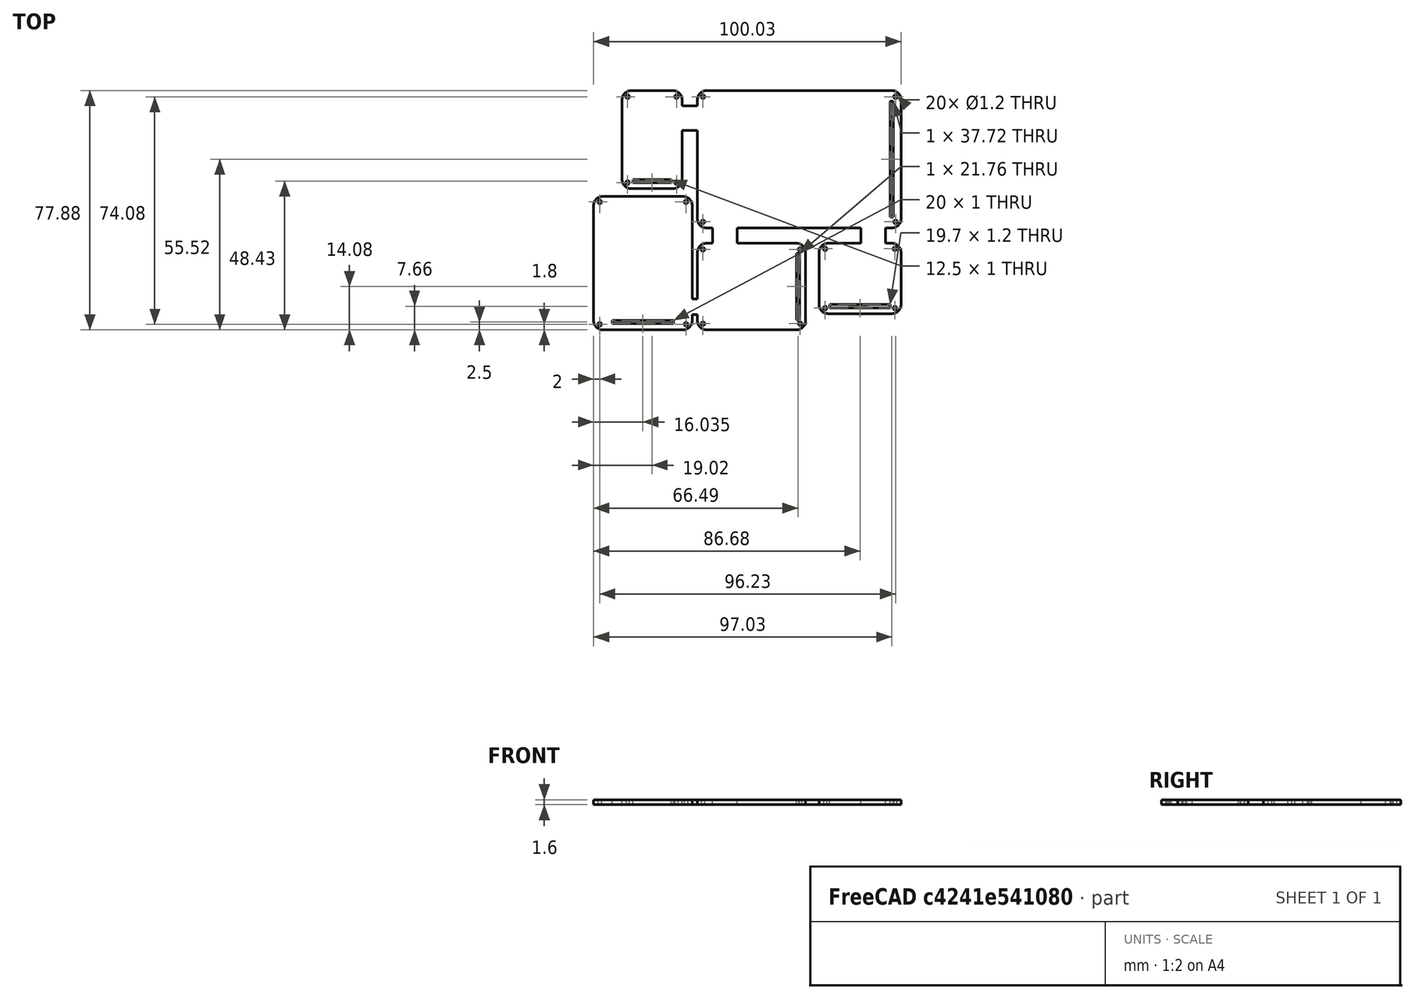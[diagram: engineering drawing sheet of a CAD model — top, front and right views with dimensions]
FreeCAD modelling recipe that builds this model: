
FCSTD DOCUMENT  (FreeCAD 0.21R33771 (Git))
Label: UINIO-Monitor
License: All rights reserved
LicenseURL: http://en.wikipedia.org/wiki/All_rights_reserved
objects: Sketcher::SketchObject×1, PartDesign::Pad×1, PartDesign::Body×1
note: 4 computed .brp shape members not serialized (recipe doc carries the construction recipe); baked Part::Feature solids carry a one-line shape summary decoded from their .brp

FEATURE [Sketcher::SketchObject] Sketch
  FullyConstrained = false
  MapMode = 5
  Support = -> [XY_Plane]
  sketch-geometry (140):
    g0: Circle CenterX=-31.33 CenterY=20.36 CenterZ=0 NormalX=0 NormalY=0 NormalZ=1 AngleXU=0 Radius=0.875
    g1: Circle CenterX=-31.33 CenterY=20.36 CenterZ=0 NormalX=0 NormalY=0 NormalZ=1 AngleXU=0 Radius=0.6
    g2: LineSegment StartX=-30.13 StartY=21.36 StartZ=0 EndX=30.13 EndY=21.36 EndZ=0
    g3: LineSegment StartX=30.13 StartY=21.36 StartZ=0 EndX=30.13 EndY=-21.36 EndZ=0
    g4: LineSegment StartX=30.13 StartY=-21.36 StartZ=0 EndX=-30.13 EndY=-21.36 EndZ=0
    g5: LineSegment StartX=-30.13 StartY=-21.36 StartZ=0 EndX=-30.13 EndY=21.36 EndZ=0
    g6: LineSegment StartX=-30.13 StartY=22.36 StartZ=0 EndX=30.13 EndY=22.36 EndZ=0
    g7: LineSegment StartX=-30.13 StartY=-22.36 StartZ=0 EndX=30.13 EndY=-22.36 EndZ=0
    g8: LineSegment StartX=33.13 StartY=19.36 StartZ=0 EndX=33.13 EndY=-19.36 EndZ=0
    g9: ArcOfCircle CenterX=30.13 CenterY=19.36 CenterZ=0 NormalX=0 NormalY=0 NormalZ=1 AngleXU=0 Radius=3 StartAngle=0 EndAngle=1.5708
    g10: ArcOfCircle CenterX=30.13 CenterY=-19.36 CenterZ=0 NormalX=0 NormalY=0 NormalZ=1 AngleXU=0 Radius=3 StartAngle=4.71239 EndAngle=6.28319
    g11: ArcOfCircle CenterX=-30.13 CenterY=-19.36 CenterZ=0 NormalX=0 NormalY=0 NormalZ=1 AngleXU=0 Radius=3 StartAngle=3.14159 EndAngle=4.71239
    g12: ArcOfCircle CenterX=-30.13 CenterY=19.3596 CenterZ=0 NormalX=0 NormalY=0 NormalZ=1 AngleXU=0 Radius=3.00035 StartAngle=1.5708 EndAngle=3.12625
    g13: LineSegment StartX=29.63 StartY=18.86 StartZ=0 EndX=30.63 EndY=18.86 EndZ=0
    g14: LineSegment StartX=30.63 StartY=18.86 StartZ=0 EndX=30.63 EndY=-18.86 EndZ=0
    g15: LineSegment StartX=30.63 StartY=-18.86 StartZ=0 EndX=29.63 EndY=-18.86 EndZ=0
    g16: LineSegment StartX=29.63 StartY=-18.86 StartZ=0 EndX=29.63 EndY=18.86 EndZ=0
    g17: Circle CenterX=-31.33 CenterY=-20.36 CenterZ=0 NormalX=0 NormalY=0 NormalZ=1 AngleXU=0 Radius=0.875
    g18: Circle CenterX=-31.33 CenterY=-20.36 CenterZ=0 NormalX=0 NormalY=0 NormalZ=1 AngleXU=0 Radius=0.6
    g19: Circle CenterX=31.33 CenterY=20.36 CenterZ=0 NormalX=0 NormalY=0 NormalZ=1 AngleXU=0 Radius=0.875
    g20: Circle CenterX=31.33 CenterY=20.36 CenterZ=0 NormalX=0 NormalY=0 NormalZ=1 AngleXU=0 Radius=0.6
    g21: Circle CenterX=31.33 CenterY=-20.36 CenterZ=0 NormalX=0 NormalY=0 NormalZ=1 AngleXU=0 Radius=0.875
    g22: Circle CenterX=31.33 CenterY=-20.36 CenterZ=0 NormalX=0 NormalY=0 NormalZ=1 AngleXU=0 Radius=0.6
    g23: LineSegment StartX=-30.13 StartY=-28.36 StartZ=0 EndX=-0.91 EndY=-28.36 EndZ=0
    g24: LineSegment StartX=-0.91 StartY=-28.36 StartZ=0 EndX=-0.91 EndY=-54.52 EndZ=0
    g25: LineSegment StartX=-0.91 StartY=-54.52 StartZ=0 EndX=-30.13 EndY=-54.52 EndZ=0
    g26: LineSegment StartX=-30.13 StartY=-54.52 StartZ=0 EndX=-30.13 EndY=-28.36 EndZ=0
    g27: LineSegment StartX=7.43 StartY=-30.36 StartZ=0 EndX=32.13 EndY=-30.36 EndZ=0
    g28: LineSegment StartX=32.13 StartY=-30.36 StartZ=0 EndX=32.13 EndY=-47.26 EndZ=0
    g29: LineSegment StartX=32.13 StartY=-47.26 StartZ=0 EndX=7.43 EndY=-47.26 EndZ=0
    g30: LineSegment StartX=7.43 StartY=-47.26 StartZ=0 EndX=7.43 EndY=-30.36 EndZ=0
    g31: LineSegment StartX=-30.13 StartY=-27.36 StartZ=0 EndX=-0.91 EndY=-27.36 EndZ=0
    g32: LineSegment StartX=2.09 StartY=-30.36 StartZ=0 EndX=2.09 EndY=-52.52 EndZ=0
    g33: LineSegment StartX=-30.13 StartY=-55.52 StartZ=0 EndX=-0.91 EndY=-55.52 EndZ=0
    g34: ArcOfCircle CenterX=-0.91 CenterY=-30.36 CenterZ=0 NormalX=0 NormalY=0 NormalZ=1 AngleXU=0 Radius=3 StartAngle=0 EndAngle=1.5708
    g35: ArcOfCircle CenterX=-0.91 CenterY=-52.52 CenterZ=0 NormalX=0 NormalY=0 NormalZ=1 AngleXU=0 Radius=3 StartAngle=4.71239 EndAngle=6.28319
    g36: ArcOfCircle CenterX=-30.13 CenterY=-52.52 CenterZ=0 NormalX=0 NormalY=0 NormalZ=1 AngleXU=0 Radius=3 StartAngle=3.14158 EndAngle=4.71239
    g37: ArcOfCircle CenterX=-30.13 CenterY=-30.36 CenterZ=0 NormalX=0 NormalY=0 NormalZ=1 AngleXU=0 Radius=3 StartAngle=1.5708 EndAngle=3.14159
    g38: Circle CenterX=-31.33 CenterY=-29.36 CenterZ=0 NormalX=0 NormalY=0 NormalZ=1 AngleXU=0 Radius=0.6
    g39: Circle CenterX=-31.33 CenterY=-29.36 CenterZ=0 NormalX=0 NormalY=0 NormalZ=1 AngleXU=0 Radius=0.875
    g40: Circle CenterX=-31.33 CenterY=-53.52 CenterZ=0 NormalX=0 NormalY=0 NormalZ=1 AngleXU=0 Radius=0.6
    g41: Circle CenterX=-31.33 CenterY=-53.52 CenterZ=0 NormalX=0 NormalY=0 NormalZ=1 AngleXU=0 Radius=0.875
    g42: Circle CenterX=0.29 CenterY=-29.36 CenterZ=0 NormalX=0 NormalY=0 NormalZ=1 AngleXU=0 Radius=0.6
    g43: Circle CenterX=0.29 CenterY=-29.36 CenterZ=0 NormalX=0 NormalY=0 NormalZ=1 AngleXU=0 Radius=0.875
    g44: Circle CenterX=0.29 CenterY=-53.52 CenterZ=0 NormalX=0 NormalY=0 NormalZ=1 AngleXU=0 Radius=0.6
    g45: Circle CenterX=0.29 CenterY=-53.52 CenterZ=0 NormalX=0 NormalY=0 NormalZ=1 AngleXU=0 Radius=0.875
    g46: LineSegment StartX=-0.91 StartY=-30.56 StartZ=0 EndX=0.09 EndY=-30.56 EndZ=0
    g47: LineSegment StartX=0.09 StartY=-30.56 StartZ=0 EndX=0.09 EndY=-52.32 EndZ=0
    g48: LineSegment StartX=0.09 StartY=-52.32 StartZ=0 EndX=-0.91 EndY=-52.32 EndZ=0
    g49: LineSegment StartX=-0.91 StartY=-52.32 StartZ=0 EndX=-0.91 EndY=-30.56 EndZ=0
    g50: LineSegment StartX=9.43 StartY=-27.36 StartZ=0 EndX=30.13 EndY=-27.36 EndZ=0
    g51: LineSegment StartX=33.13 StartY=-30.36 StartZ=0 EndX=33.13 EndY=-47.26 EndZ=0
    g52: LineSegment StartX=30.13 StartY=-50.26 StartZ=0 EndX=9.43 EndY=-50.26 EndZ=0
    g53: LineSegment StartX=6.43 StartY=-47.26 StartZ=0 EndX=6.43 EndY=-30.36 EndZ=0
    g54: ArcOfCircle CenterX=30.13 CenterY=-30.36 CenterZ=0 NormalX=0 NormalY=0 NormalZ=1 AngleXU=0 Radius=3 StartAngle=0 EndAngle=1.5708
    g55: ArcOfCircle CenterX=30.13 CenterY=-47.26 CenterZ=0 NormalX=0 NormalY=0 NormalZ=1 AngleXU=0 Radius=3 StartAngle=4.71239 EndAngle=6.28319
    g56: ArcOfCircle CenterX=9.43 CenterY=-47.26 CenterZ=0 NormalX=0 NormalY=0 NormalZ=1 AngleXU=0 Radius=3 StartAngle=3.14159 EndAngle=4.71239
    g57: ArcOfCircle CenterX=9.43 CenterY=-30.36 CenterZ=0 NormalX=0 NormalY=0 NormalZ=1 AngleXU=0 Radius=3 StartAngle=1.5708 EndAngle=3.14159
    g58: Circle CenterX=8.43 CenterY=-48.46 CenterZ=0 NormalX=0 NormalY=0 NormalZ=1 AngleXU=0 Radius=0.6
    g59: Circle CenterX=8.43 CenterY=-48.46 CenterZ=0 NormalX=0 NormalY=0 NormalZ=1 AngleXU=0 Radius=0.875
    g60: Circle CenterX=31.13 CenterY=-29.16 CenterZ=0 NormalX=0 NormalY=0 NormalZ=1 AngleXU=0 Radius=0.6
    g61: Circle CenterX=31.13 CenterY=-29.16 CenterZ=0 NormalX=0 NormalY=0 NormalZ=1 AngleXU=0 Radius=0.875
    g62: Circle CenterX=31.13 CenterY=-48.46 CenterZ=0 NormalX=0 NormalY=0 NormalZ=1 AngleXU=0 Radius=0.6
    g63: Circle CenterX=31.13 CenterY=-48.46 CenterZ=0 NormalX=0 NormalY=0 NormalZ=1 AngleXU=0 Radius=0.898498
    g64: Circle CenterX=8.43 CenterY=-29.16 CenterZ=0 NormalX=0 NormalY=0 NormalZ=1 AngleXU=0 Radius=0.6
    g65: Circle CenterX=8.43 CenterY=-29.16 CenterZ=0 NormalX=0 NormalY=0 NormalZ=1 AngleXU=0 Radius=0.875
    g66: LineSegment StartX=-30.13 StartY=-22.36 StartZ=0 EndX=-28.13 EndY=-22.36 EndZ=0
    g67: LineSegment StartX=-28.13 StartY=-22.36 StartZ=0 EndX=-28.13 EndY=-27.36 EndZ=0
    g68: LineSegment StartX=-28.13 StartY=-27.36 StartZ=0 EndX=-30.13 EndY=-27.36 EndZ=0
    g69: LineSegment StartX=20.13 StartY=-27.36 StartZ=0 EndX=20.13 EndY=-22.36 EndZ=0
    g70: LineSegment StartX=28.13 StartY=-22.36 StartZ=0 EndX=30.13 EndY=-22.36 EndZ=0
    g71: LineSegment StartX=28.13 StartY=-22.36 StartZ=0 EndX=28.13 EndY=-27.36 EndZ=0
    g72: LineSegment StartX=28.13 StartY=-27.36 StartZ=0 EndX=30.13 EndY=-27.36 EndZ=0
    g73: LineSegment StartX=9.93 StartY=-47.26 StartZ=0 EndX=29.63 EndY=-47.26 EndZ=0
    g74: LineSegment StartX=29.63 StartY=-47.26 StartZ=0 EndX=29.63 EndY=-48.46 EndZ=0
    g75: LineSegment StartX=29.63 StartY=-48.46 StartZ=0 EndX=9.93 EndY=-48.46 EndZ=0
    g76: LineSegment StartX=9.93 StartY=-48.46 StartZ=0 EndX=9.93 EndY=-47.26 EndZ=0
    g77: LineSegment StartX=-54.63 StartY=21.36 StartZ=0 EndX=-41.13 EndY=21.36 EndZ=0
    g78: LineSegment StartX=-41.13 StartY=21.36 StartZ=0 EndX=-41.13 EndY=-6.59 EndZ=0
    g79: LineSegment StartX=-41.13 StartY=-6.59 StartZ=0 EndX=-54.63 EndY=-6.59 EndZ=0
    g80: LineSegment StartX=-54.63 StartY=-6.59 StartZ=0 EndX=-54.63 EndY=21.36 EndZ=0
    g81: LineSegment StartX=-54.63 StartY=22.36 StartZ=0 EndX=-41.13 EndY=22.36 EndZ=0
    g82: LineSegment StartX=-41.13 StartY=-9.59 StartZ=0 EndX=-54.63 EndY=-9.59 EndZ=0
    g83: LineSegment StartX=-57.63 StartY=-6.59 StartZ=0 EndX=-57.63 EndY=19.36 EndZ=0
    g84: ArcOfCircle CenterX=-54.63 CenterY=-6.59 CenterZ=0 NormalX=0 NormalY=0 NormalZ=1 AngleXU=0 Radius=3 StartAngle=3.14159 EndAngle=4.71239
    g85: ArcOfCircle CenterX=-41.13 CenterY=-6.59 CenterZ=0 NormalX=0 NormalY=0 NormalZ=1 AngleXU=0 Radius=3 StartAngle=4.71239 EndAngle=6.28319
    g86: ArcOfCircle CenterX=-41.13 CenterY=19.36 CenterZ=0 NormalX=0 NormalY=0 NormalZ=1 AngleXU=0 Radius=3 StartAngle=4e-16 EndAngle=1.5708
    g87: ArcOfCircle CenterX=-54.63 CenterY=19.36 CenterZ=0 NormalX=0 NormalY=0 NormalZ=1 AngleXU=0 Radius=3 StartAngle=1.5708 EndAngle=3.14159
    g88: LineSegment StartX=-38.13 StartY=-6.59 StartZ=0 EndX=-38.13 EndY=9.36 EndZ=0
    g89: LineSegment StartX=-38.13 StartY=19.36 StartZ=0 EndX=-38.13 EndY=17.36 EndZ=0
    g90: LineSegment StartX=-33.13 StartY=19.4057 StartZ=0 EndX=-33.13 EndY=17.36 EndZ=0
    g91: LineSegment StartX=-38.13 StartY=17.36 StartZ=0 EndX=-33.13 EndY=17.36 EndZ=0
    g92: LineSegment StartX=-33.13 StartY=9.36 StartZ=0 EndX=-38.13 EndY=9.36 EndZ=0
    g93: LineSegment StartX=-54.13 StartY=-6.59 StartZ=0 EndX=-41.63 EndY=-6.59 EndZ=0
    g94: LineSegment StartX=-41.63 StartY=-6.59 StartZ=0 EndX=-41.63 EndY=-7.59 EndZ=0
    g95: LineSegment StartX=-41.63 StartY=-7.59 StartZ=0 EndX=-54.13 EndY=-7.59 EndZ=0
    g96: LineSegment StartX=-54.13 StartY=-7.59 StartZ=0 EndX=-54.13 EndY=-6.59 EndZ=0
    g97: Circle CenterX=-55.83 CenterY=20.36 CenterZ=0 NormalX=0 NormalY=0 NormalZ=1 AngleXU=0 Radius=0.875
    g98: Circle CenterX=-55.83 CenterY=20.36 CenterZ=0 NormalX=0 NormalY=0 NormalZ=1 AngleXU=0 Radius=0.6
    g99: Circle CenterX=-39.93 CenterY=-7.59 CenterZ=0 NormalX=0 NormalY=0 NormalZ=1 AngleXU=0 Radius=0.875
    g100: Circle CenterX=-39.93 CenterY=-7.59 CenterZ=0 NormalX=0 NormalY=0 NormalZ=1 AngleXU=0 Radius=0.6
    g101: Circle CenterX=-55.83 CenterY=-7.59 CenterZ=0 NormalX=0 NormalY=0 NormalZ=1 AngleXU=0 Radius=0.875
    g102: Circle CenterX=-55.83 CenterY=-7.59 CenterZ=0 NormalX=0 NormalY=0 NormalZ=1 AngleXU=0 Radius=0.6
    g103: Circle CenterX=-39.93 CenterY=20.36 CenterZ=0 NormalX=0 NormalY=0 NormalZ=1 AngleXU=0 Radius=0.875
    g104: Circle CenterX=-39.93 CenterY=20.36 CenterZ=0 NormalX=0 NormalY=0 NormalZ=1 AngleXU=0 Radius=0.6
    g105: LineSegment StartX=-20.13 StartY=-22.36 StartZ=0 EndX=-20.13 EndY=-27.36 EndZ=0
    g106: LineSegment StartX=20.13 StartY=-22.36 StartZ=0 EndX=-20.13 EndY=-22.36 EndZ=0
    g107: LineSegment StartX=-20.13 StartY=-27.36 StartZ=0 EndX=-0.91 EndY=-27.36 EndZ=0
    g108: LineSegment StartX=9.43 StartY=-27.36 StartZ=0 EndX=20.13 EndY=-27.36 EndZ=0
    g109: LineSegment StartX=-33.13 StartY=9.36 StartZ=0 EndX=-33.13 EndY=-17.86 EndZ=0
    g110: LineSegment StartX=-33.13 StartY=-17.86 StartZ=0 EndX=-33.13 EndY=-19.36 EndZ=0
    g111: LineSegment StartX=-65.9 StartY=-15.09 StartZ=0 EndX=-35.83 EndY=-15.09 EndZ=0
    g112: LineSegment StartX=-35.83 StartY=-15.09 StartZ=0 EndX=-35.83 EndY=-52.52 EndZ=0
    g113: LineSegment StartX=-35.83 StartY=-52.52 StartZ=0 EndX=-65.9 EndY=-52.52 EndZ=0
    g114: LineSegment StartX=-65.9 StartY=-52.52 StartZ=0 EndX=-65.9 EndY=-15.09 EndZ=0
    g115: LineSegment StartX=-63.9 StartY=-12.09 StartZ=0 EndX=-37.83 EndY=-12.09 EndZ=0
    g116: LineSegment StartX=-37.83 StartY=-55.52 StartZ=0 EndX=-63.9 EndY=-55.52 EndZ=0
    g117: LineSegment StartX=-66.9 StartY=-52.52 StartZ=0 EndX=-66.9 EndY=-15.09 EndZ=0
    g118: ArcOfCircle CenterX=-37.83 CenterY=-52.52 CenterZ=0 NormalX=0 NormalY=0 NormalZ=1 AngleXU=0 Radius=3 StartAngle=4.71239 EndAngle=6.28319
    g119: ArcOfCircle CenterX=-63.9 CenterY=-52.52 CenterZ=0 NormalX=0 NormalY=0 NormalZ=1 AngleXU=0 Radius=3 StartAngle=3.14159 EndAngle=4.71239
    g120: ArcOfCircle CenterX=-63.9 CenterY=-15.09 CenterZ=0 NormalX=0 NormalY=0 NormalZ=1 AngleXU=0 Radius=3 StartAngle=1.5708 EndAngle=3.14159
    g121: ArcOfCircle CenterX=-37.83 CenterY=-15.09 CenterZ=0 NormalX=0 NormalY=0 NormalZ=1 AngleXU=0 Radius=3 StartAngle=2e-16 EndAngle=1.5708
    g122: LineSegment StartX=-60.865 StartY=-52.52 StartZ=0 EndX=-40.865 EndY=-52.52 EndZ=0
    g123: LineSegment StartX=-40.865 StartY=-52.52 StartZ=0 EndX=-40.865 EndY=-53.52 EndZ=0
    g124: LineSegment StartX=-40.865 StartY=-53.52 StartZ=0 EndX=-60.865 EndY=-53.52 EndZ=0
    g125: LineSegment StartX=-60.865 StartY=-53.52 StartZ=0 EndX=-60.865 EndY=-52.52 EndZ=0
    g126: LineSegment StartX=-33.13 StartY=-30.36 StartZ=0 EndX=-33.13 EndY=-45.52 EndZ=0
    g127: LineSegment StartX=-33.13 StartY=-52.52 StartZ=0 EndX=-33.13 EndY=-50.52 EndZ=0
    g128: LineSegment StartX=-34.83 StartY=-15.09 StartZ=0 EndX=-34.83 EndY=-45.52 EndZ=0
    g129: LineSegment StartX=-33.13 StartY=-45.52 StartZ=0 EndX=-34.83 EndY=-45.52 EndZ=0
    g130: LineSegment StartX=-34.83 StartY=-52.52 StartZ=0 EndX=-34.83 EndY=-50.52 EndZ=0
    g131: LineSegment StartX=-33.13 StartY=-50.52 StartZ=0 EndX=-34.83 EndY=-50.52 EndZ=0
    g132: Circle CenterX=-64.9 CenterY=-13.89 CenterZ=0 NormalX=0 NormalY=0 NormalZ=1 AngleXU=0 Radius=0.6
    g133: Circle CenterX=-64.9 CenterY=-13.89 CenterZ=0 NormalX=0 NormalY=0 NormalZ=1 AngleXU=0 Radius=0.875
    g134: Circle CenterX=-36.83 CenterY=-13.89 CenterZ=0 NormalX=0 NormalY=0 NormalZ=1 AngleXU=0 Radius=0.6
    g135: Circle CenterX=-36.83 CenterY=-13.89 CenterZ=0 NormalX=0 NormalY=0 NormalZ=1 AngleXU=0 Radius=0.875
    g136: Circle CenterX=-36.83 CenterY=-53.72 CenterZ=0 NormalX=0 NormalY=0 NormalZ=1 AngleXU=0 Radius=0.875
    g137: Circle CenterX=-36.83 CenterY=-53.72 CenterZ=0 NormalX=0 NormalY=0 NormalZ=1 AngleXU=0 Radius=0.6
    g138: Circle CenterX=-64.9 CenterY=-53.72 CenterZ=0 NormalX=0 NormalY=0 NormalZ=1 AngleXU=0 Radius=0.875
    g139: Circle CenterX=-64.9 CenterY=-53.72 CenterZ=0 NormalX=0 NormalY=0 NormalZ=1 AngleXU=0 Radius=0.6
  constraints (358):
    c: Diameter(g0) = 1.75
    c: Coincident(g0,g1)
    c: Diameter(g1) = 1.2
    c: Coincident(g2,g3)
    c: Coincident(g3,g4)
    c: Coincident(g4,g5)
    c: Coincident(g5,g2)
    c: Horizontal(g2)
    c: Horizontal(g4)
    c: Vertical(g3)
    c: Vertical(g5)
    c: DistanceX(g2,g2) = 60.26
    c: DistanceY(g3,g3) = 42.72
    c: Symmetric(g4,g2,g-1)
    c: Horizontal(g6)
    c: Horizontal(g7)
    c: Vertical(g8)
    c: Tangent(g6,g9) = 1.5708
    c: Tangent(g8,g9) = 1.5708
    c: Tangent(g7,g10) = -1.5708
    c: Tangent(g8,g10) = 1.5708
    c: Tangent(g7,g11) = -1.5708
    c: Tangent(g6,g12) = 1.5708
    c: Distance(g8,g3) = 3
    c: Vertical(g7,g4)
    c: Vertical(g6,g2)
    c: Distance(g6,g2) = 1
    c: Distance(g7,g4) = 1
    c: Vertical(g6,g2)
    c: Vertical(g7,g3)
    c: Coincident(g13,g14)
    c: Coincident(g14,g15)
    c: Coincident(g15,g16)
    c: Coincident(g16,g13)
    c: Horizontal(g13)
    c: Horizontal(g15)
    c: Vertical(g14)
    c: Vertical(g16)
    c: Distance(g13,g2) = 2.5
    c: Distance(g15,g4) = 2.5
    c: DistanceX(g13,g13) = 1
    c: Distance(g13,g3) = 0.5
    c: Distance(g1,g6) = 2
    c: Equal(g0,g17) = 1.75
    c: Coincident(g17,g18)
    c: Equal(g1,g18) = 1.2
    c: Distance(g18,g7) = 2
    c: Coincident(g19,g20)
    c: Coincident(g21,g22)
    c: Distance(g20,g6) = 2
    c: Distance(g20,g3) = 1.2
    c: Distance(g22,g3) = 1.2
    c: Distance(g22,g7) = 2
    c: Coincident(g23,g24)
    c: Coincident(g24,g25)
    c: Coincident(g25,g26)
    c: Coincident(g26,g23)
    c: Horizontal(g23)
    c: Horizontal(g25)
    c: Vertical(g24)
    c: Vertical(g26)
    c: Coincident(g27,g28)
    c: Coincident(g28,g29)
    c: Coincident(g29,g30)
    c: Coincident(g30,g27)
    c: Horizontal(g27)
    c: Horizontal(g29)
    c: Vertical(g28)
    c: Vertical(g30)
    c: DistanceX(g23,g23) = 29.22
    c: DistanceY(g26,g26) = 26.16
    c: Horizontal(g31)
    c: Vertical(g32)
    c: Horizontal(g33)
    c: Tangent(g31,g34) = 1.5708
    c: Tangent(g32,g34) = 1.5708
    c: Tangent(g32,g35) = 1.5708
    c: Tangent(g33,g35) = -1.5708
    c: Tangent(g33,g36) = -1.5708
    c: Tangent(g31,g37) = 1.5708
    c: Distance(g32,g24) = 3
    c: Vertical(g23,g31)
    c: Vertical(g33,g24)
    c: Vertical(g33,g25)
    c: Vertical(g31,g23)
    c: Distance(g33,g25) = 1
    c: Distance(g31,g23) = 1
    c: Vertical(g31,g7)
    c: Distance(g31,g7) = 5
    c: Distance(g18,g5) = 1.2
    c: Distance(g1,g5) = 1.2
    c: Coincident(g39,g38)
    c: Coincident(g41,g40)
    c: Coincident(g43,g42)
    c: Coincident(g45,g44)
    c: Distance(g38,g31) = 2
    c: Distance(g38,g26) = 1.2
    c: Distance(g40,g26) = 1.2
    c: Distance(g40,g33) = 2
    c: Distance(g44,g33) = 2
    c: Distance(g44,g24) = 1.2
    c: Distance(g42,g31) = 2
    c: Distance(g42,g24) = 1.2
    c: Coincident(g46,g47)
    c: Coincident(g47,g48)
    c: Coincident(g48,g49)
    c: Coincident(g49,g46)
    c: Horizontal(g46)
    c: Horizontal(g48)
    c: Vertical(g47)
    c: Vertical(g49)
    c: DistanceX(g46,g46) = 1
    c: PointOnObject(g46,g24)
    c: Distance(g46,g23) = 2.2
    c: Distance(g48,g25) = 2.2
    c: DistanceX(g27,g27) = 24.7
    c: DistanceY(g30,g30) = 16.9
    c: Horizontal(g50)
    c: Horizontal(g52)
    c: Vertical(g51)
    c: Vertical(g53)
    c: Tangent(g51,g54) = 1.5708
    c: Tangent(g50,g54) = 1.5708
    c: Tangent(g51,g55) = 1.5708
    c: Tangent(g52,g55) = 1.5708
    c: Tangent(g53,g56) = 1.5708
    c: Tangent(g52,g56) = 1.5708
    c: Tangent(g50,g57) = 1.5708
    c: Tangent(g53,g57) = 1.5708
    c: Distance(g52,g29) = 3
    c: Horizontal(g51,g27)
    c: Horizontal(g27,g53)
    c: Distance(g53,g30) = 1
    c: Distance(g51,g28) = 1
    c: Distance(g50,g27) = 3
    c: Horizontal(g53,g29)
    c: Horizontal(g51,g28)
    c: Vertical(g50,g7)
    c: Distance(g50,g7) = 5
    c: Coincident(g59,g58)
    c: Coincident(g61,g60)
    c: Coincident(g63,g62)
    c: Coincident(g65,g64)
    c: Distance(g64,g27) = 1.2
    c: Distance(g64,g53) = 2
    c: Distance(g60,g51) = 2
    c: Distance(g60,g27) = 1.2
    c: Distance(g58,g53) = 2
    c: Distance(g58,g29) = 1.2
    c: Distance(g62,g29) = 1.2
    c: Distance(g62,g51) = 2
    c: Horizontal(g66)
    c: Coincident(g66,g67)
    c: Vertical(g67)
    c: Coincident(g67,g68)
    c: Horizontal(g68)
    c: DistanceY(g67,g67) = 5
    c: Horizontal(g105,g67)
    c: Horizontal(g105,g66)
    c: Distance(g105,g66) = 8
    c: Equal(g68,g66)
    c: Vertical(g69)
    c: Horizontal(g70)
    c: Coincident(g70,g71)
    c: Coincident(g71,g72)
    c: Horizontal(g72)
    c: Vertical(g71)
    c: Horizontal(g71,g69)
    c: Horizontal(g69,g70)
    c: Distance(g70,g69) = 8
    c: Equal(g72,g70)
    c: Coincident(g68,g37)
    c: PointOnObject(g70,g10)
    c: Coincident(g73,g74)
    c: Coincident(g74,g75)
    c: Coincident(g75,g76)
    c: Coincident(g76,g73)
    c: Horizontal(g73)
    c: Horizontal(g75)
    c: Vertical(g74)
    c: Vertical(g76)
    c: PointOnObject(g73,g29)
    c: DistanceY(g76,g76) = 1.2
    c: Distance(g73,g30) = 2.5
    c: Distance(g73,g28) = 2.5
    c: Coincident(g77,g78)
    c: Coincident(g78,g79)
    c: Coincident(g79,g80)
    c: Coincident(g80,g77)
    c: Horizontal(g77)
    c: Horizontal(g79)
    c: Vertical(g78)
    c: Vertical(g80)
    c: DistanceX(g77,g77) = 13.5
    c: DistanceY(g80,g80) = 27.95
    c: Horizontal(g81)
    c: Horizontal(g82)
    c: Distance(g77,g81) = 1
    c: Distance(g78,g82) = 3
    c: Distance(g77,g83) = 3
    c: Tangent(g82,g84) = 1.5708
    c: Tangent(g83,g84) = 1.5708
    c: Tangent(g82,g85) = 1.5708
    c: Tangent(g81,g86) = 1.5708
    c: Tangent(g81,g87) = 1.5708
    c: Tangent(g83,g87) = 1.5708
    c: Radius(g87) = 3
    c: Radius(g84) = 3
    c: Radius(g85) = 3
    c: Radius(g86) = 3
    c: Coincident(g88,g85)
    c: Vertical(g88)
    c: Coincident(g89,g86)
    c: Vertical(g89)
    c: Coincident(g90,g12)
    c: Vertical(g90)
    c: Horizontal(g90,g89)
    c: Horizontal(g92,g88)
    c: Coincident(g91,g89)
    c: Coincident(g91,g90)
    c: Coincident(g92,g88)
    c: Distance(g90,g92) = 8
    c: Vertical(g88,g89)
    c: Vertical(g92,g90)
    c: Distance(g11,g5) = 3
    c: Distance(g77,g89) = 3
    c: Distance(g11,g66) = 2
    c: Distance(g10,g70) = 2
    c: Distance(g89,g90) = 5
    c: Angle(g86) = 1.5708
    c: Angle(g85) = 1.5708
    c: Radius(g11) = 3
    c: Coincident(g93,g94)
    c: Coincident(g94,g95)
    c: Coincident(g95,g96)
    c: Coincident(g96,g93)
    c: Horizontal(g93)
    c: Horizontal(g95)
    c: Vertical(g94)
    c: Vertical(g96)
    c: DistanceY(g94,g94) = 1
    c: Distance(g93,g94) = 12.5
    c: PointOnObject(g93,g79)
    c: Distance(g84,g96) = 0.5
    c: Diameter(g97) = 1.75
    c: Coincident(g97,g98)
    c: Diameter(g98) = 1.2
    c: Diameter(g99) = 1.75
    c: Coincident(g99,g100)
    c: Diameter(g100) = 1.2
    c: Diameter(g101) = 1.75
    c: Coincident(g101,g102)
    c: Diameter(g102) = 1.2
    c: Diameter(g103) = 1.75
    c: Coincident(g103,g104)
    c: Diameter(g104) = 1.2
    c: Distance(g104,g81) = 2
    c: Distance(g104,g78) = 1.2
    c: Distance(g98,g80) = 1.2
    c: Distance(g98,g81) = 2
    c: Distance(g100,g82) = 2
    c: Distance(g100,g78) = 1.2
    c: Distance(g102,g82) = 2
    c: Distance(g102,g80) = 1.2
    c: Horizontal(g81,g6)
    c: Vertical(g83)
    c: Distance(g89,g86) = 2
    c: Vertical(g105)
    c: Coincident(g106,g69)
    c: Coincident(g106,g105)
    c: Horizontal(g106)
    c: Coincident(g107,g105)
    c: Coincident(g107,g34)
    c: Coincident(g108,g57)
    c: Coincident(g108,g69)
    c: Horizontal(g108)
    c: Coincident(g92,g109)
    c: Vertical(g109)
    c: Coincident(g110,g11)
    c: Vertical(g110)
    c: DistanceY(g110,g110) = 1.5
    c: Coincident(g111,g112)
    c: Coincident(g112,g113)
    c: Coincident(g113,g114)
    c: Coincident(g114,g111)
    c: Horizontal(g111)
    c: Horizontal(g113)
    c: Vertical(g112)
    c: Vertical(g114)
    c: DistanceX(g111,g111) = 30.07
    c: DistanceY(g114,g114) = 37.43
    c: Horizontal(g115)
    c: Horizontal(g116)
    c: Vertical(g117)
    c: Distance(g113,g116) = 3
    c: Distance(g111,g117) = 1
    c: Tangent(g116,g118) = 1.5708
    c: Tangent(g117,g119) = 1.5708
    c: Tangent(g116,g119) = 1.5708
    c: Tangent(g117,g120) = 1.5708
    c: Tangent(g115,g120) = 1.5708
    c: Tangent(g115,g121) = 1.5708
    c: Radius(g120) = 3
    c: Radius(g121) = 3
    c: Radius(g119) = 3
    c: Radius(g118) = 3
    c: Distance(g115,g111) = 3
    c: Coincident(g122,g123)
    c: Coincident(g123,g124)
    c: Coincident(g124,g125)
    c: Coincident(g125,g122)
    c: Horizontal(g122)
    c: Horizontal(g124)
    c: Vertical(g123)
    c: DistanceX(g122,g122) = 20
    c: Distance(g122,g112) = 5.035
    c: Coincident(g110,g109)
    c: Horizontal(g116,g33)
    c: Coincident(g126,g37)
    c: Vertical(g126)
    c: Coincident(g127,g36)
    c: Vertical(g127)
    c: Coincident(g128,g121)
    c: Vertical(g128)
    c: Coincident(g129,g126)
    c: Coincident(g129,g128)
    c: Horizontal(g129)
    c: Coincident(g130,g118)
    c: Vertical(g130)
    c: Coincident(g131,g127)
    c: Coincident(g131,g130)
    c: Horizontal(g131)
    c: Equal(g130,g127)
    c: Distance(g127,g126) = 5
    c: Distance(g36,g131) = 2
    c: Vertical(g127,g126)
    c: Vertical(g130,g128)
    c: Distance(g127,g130) = 1.7
    c: Vertical(g37,g11)
    c: Distance(g111,g128) = 1
    c: Angle(g121) = 1.5708
    c: Coincident(g133,g132)
    c: Coincident(g135,g134)
    c: Coincident(g136,g137)
    c: Coincident(g138,g139)
    c: PointOnObject(g122,g113)
    c: Distance(g124,g122) = 1
    c: Distance(g137,g113) = 1.2
    c: Distance(g137,g130) = 2
    c: Distance(g139,g113) = 1.2
    c: Distance(g139,g117) = 2
    c: Distance(g132,g111) = 1.2
    c: Distance(g132,g117) = 2
    c: Distance(g134,g128) = 2
    c: Distance(g134,g111) = 1.2
    c: Distance(g124,g123) = 20
    c: Radius(g36) = 3
    c: Angle(g37) = 1.5708
FEATURE [PartDesign::Pad] Pad
  Direction = (0,0,1)
  Length = 1.6
  Length2 = 10
  Profile = -> Sketch
  ReferenceAxis = -> Sketch [N_Axis]
  Type = 0
FEATURE [PartDesign::Body] Body
  Group = -> [Sketch,Pad]
  Origin = -> Origin
  Tip = -> Pad
